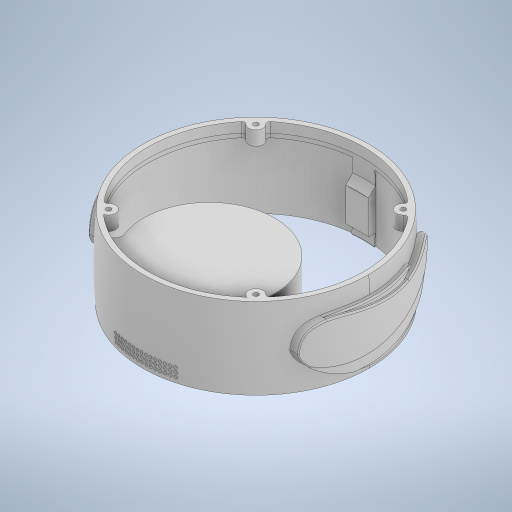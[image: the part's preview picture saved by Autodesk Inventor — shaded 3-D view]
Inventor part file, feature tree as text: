
AUTODESK INVENTOR PART (.ipt)
format: ipt  version: 2023 (Build 270158000, 158)  size: 2,226,176 bytes
history: native  units: mm
features: sketch x26, extrude x25, revolve x6, fillet x6, projected_geometry x6, other x4, mirror x3, chamfer x2, pattern_circular x1, hole x1
ambient origin geometry x8: Origin, YZ Plane, XZ Plane, XY Plane, X Axis, Y Axis, Z Axis, Center Point
bodies: Body1 (feature_tree)
feature tree (80):
  other  "솔리드1"
  revolve  "회전1"
  sketch  "스케치2"
  revolve  "회전2"
  revolve  "회전3"
  extrude  "돌출3"  Depth=120.0mm
  extrude  "돌출4"  Depth=140.0mm
  chamfer  "모따기1"  Distance=60.0mm
  fillet  "모깎기1"  Radius=130.0mm
  extrude  "돌출5"  Depth=160.0mm
  fillet  "모깎기2"  [1 undecoded]
  fillet  "모깎기3"  Radius=120.0mm
  extrude  "돌출6"  Depth=141.0mm
  other  "작업 평면2"
  extrude  "돌출7"  TaperAngle=90.0deg  [1 undecoded]
  mirror  "미러1"
  extrude  "돌출9"  Depth=4.0mm
  extrude  "돌출10"  TaperAngle=90.0deg  [1 undecoded]
  mirror  "미러2"
  sketch  "스케치13"
  extrude  "돌출11"  Depth=10.0mm
  extrude  "돌출12"  Depth=371.75mm TaperAngle=0.0deg
  sketch  "스케치15"
  extrude  "돌출13"  Depth=25.0mm
  extrude  "돌출14"  Depth=140.0mm
  pattern_circular  "원형 패턴1"  [2 undecoded]
  extrude  "돌출15"  Depth=103.5mm TaperAngle=0.0deg
  fillet  "모깎기4"  Radius=5.0mm
  other  "작업 평면4"
  extrude  "돌출16"  Depth=2.0mm
  chamfer  "모따기2"  Distance=90.0mm
  extrude  "돌출17"  Depth=103.5mm TaperAngle=0.0deg
  extrude  "돌출18"  Depth=1.0mm
  extrude  "돌출19"  Depth=0.5mm
  extrude  "돌출20"  Depth=7.0mm TaperAngle=0.0deg
  hole  "구멍1"  [1 undecoded]
  fillet  "모깎기5"  Radius=50.0mm
  extrude  "돌출21"  Depth=27.25mm TaperAngle=0.0deg
  extrude  "돌출22"  Depth=25.0mm
  extrude  "돌출23"  Depth=10.0mm TaperAngle=0.0deg
  other  "작업 평면5"
  sketch  "스케치27"
  sketch  "스케치28"
  sketch  "스케치29"
  extrude  "돌출25"  Depth=2.0mm
  revolve  "회전4"
  extrude  "돌출26"  Depth=18.0mm
  revolve  "회전5"
  extrude  "돌출27"  Depth=40.0mm TaperAngle=360.0deg
  revolve  "회전6"
  fillet  "모깎기11"  Radius=10.0mm
  mirror  "미러3"
  extrude  "돌출28"  Depth=77.0mm
  extrude  "돌출29"  Depth=77.0mm
  sketch  "스케치1"
  sketch  "스케치3"
  projected_geometry  "투영된 루프1"
  sketch  "스케치5"
  sketch  "스케치6"
  sketch  "스케치7"
  sketch  "스케치8"
  projected_geometry  "투영된 루프2"
  sketch  "스케치9"
  sketch  "스케치11"
  sketch  "스케치12"
  sketch  "스케치16"
  sketch  "스케치17"
  sketch  "스케치18"
  sketch  "스케치20"
  sketch  "스케치21"
  sketch  "스케치22"
  sketch  "스케치23"
  projected_geometry  "투영된 루프3"
  sketch  "스케치24"
  sketch  "스케치25"
  projected_geometry  "투영된 루프4"
  sketch  "스케치26"
  sketch  "스케치30"
  projected_geometry  "투영된 루프6"
  projected_geometry  "투영된 루프7"
note: 6 required parameter values undecoded (feature->parameter linkage not recoverable at this tier; creation-order binding heuristic only, values carry confidence <= 0.55)
